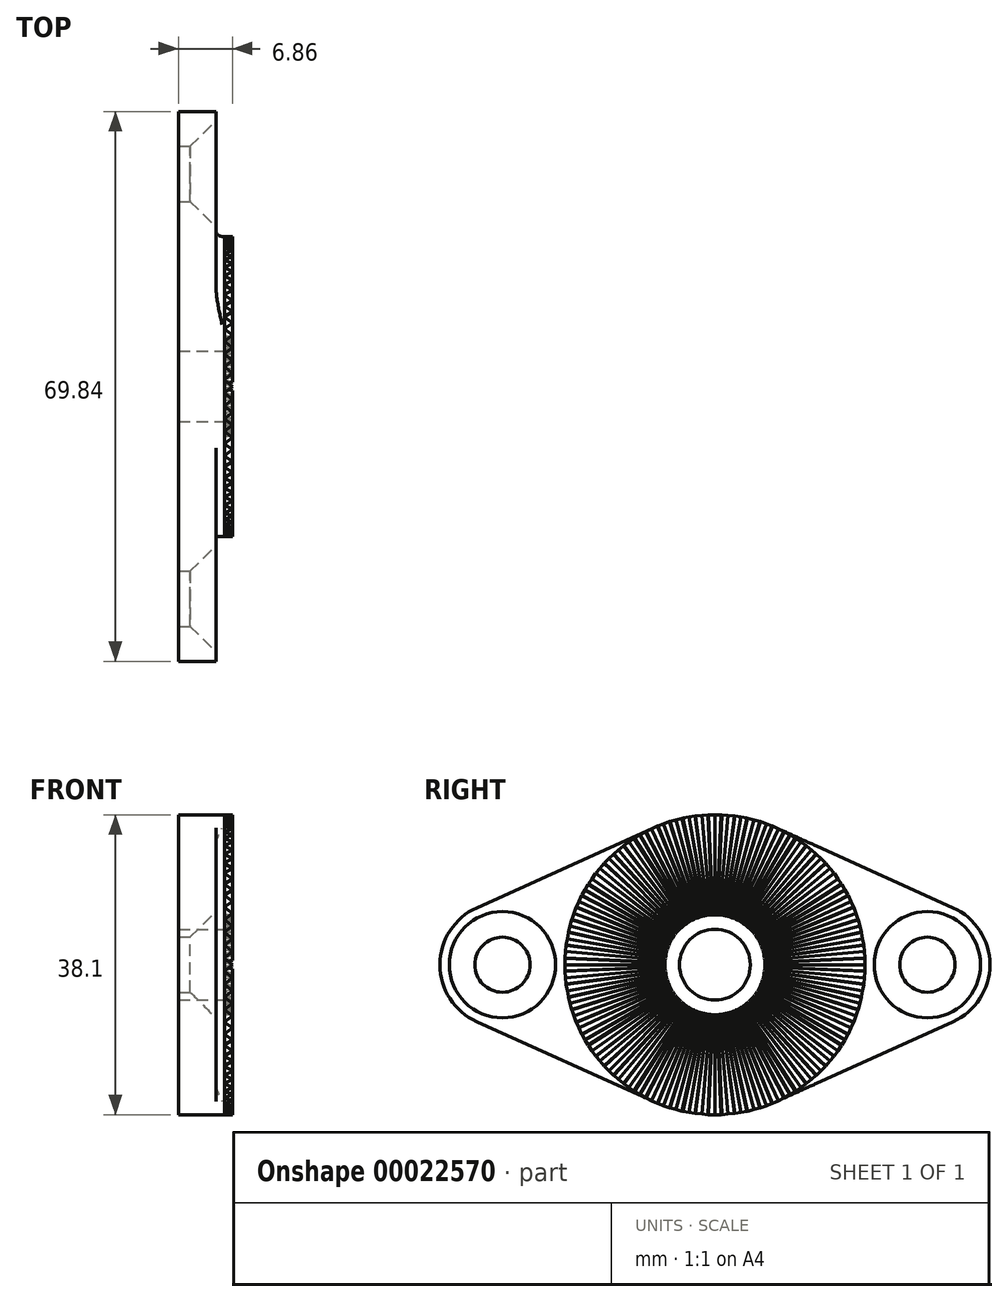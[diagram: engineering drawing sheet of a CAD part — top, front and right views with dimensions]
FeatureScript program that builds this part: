
annotation { "Feature Type Name" : "Feature", "Feature Type Description" : "" }
export const myFeature = defineFeature(function(context is Context, id is Id, definition is map)
    precondition{}
    {
        {
            var Q0;
            Q0=qCreatedBy(makeId("Right.planeOp"),FACE);
            var sketch = newSketch(context, id + "F0", { "sketchPlane" : qUnion([Q0])});
            skArc(sketch, "E0", {"start": v(-7.84, -17.36) * mm, "mid": v(0, -19.05) * mm, "end": v(7.84, -17.36) * mm});
            skLineSegment(sketch, "E1", {"start": v(-77.57, 0) * mm, "end": v(77.57, 0) * mm, "construction": true});
            skArc(sketch, "E2", {"start": v(-30.26, 7.23) * mm, "mid": v(-34.92, 0) * mm, "end": v(-30.26, -7.23) * mm});
            skArc(sketch, "E3", {"start": v(30.26, -7.23) * mm, "mid": v(34.92, 0) * mm, "end": v(30.26, 7.23) * mm});
            skLineSegment(sketch, "E4", {"start": v(-30.26, 7.23) * mm, "end": v(-7.84, 17.36) * mm});
            skLineSegment(sketch, "E5", {"start": v(-30.26, -7.23) * mm, "end": v(-7.84, -17.36) * mm});
            skLineSegment(sketch, "E6", {"start": v(30.26, -7.23) * mm, "end": v(7.84, -17.36) * mm});
            skLineSegment(sketch, "E7", {"start": v(30.26, 7.23) * mm, "end": v(7.84, 17.36) * mm});
            skArc(sketch, "E8.trimOffspring", {"start": v(7.84, 17.36) * mm, "mid": v(0, 19.05) * mm, "end": v(-7.84, 17.36) * mm});
            skSolve(sketch);
        }
        {
            var Q0;
            Q0=qSketchRegion(id+"F0",true);
            extrude(context, id + "F1", {"entities" : qUnion([Q0]), "depth" : 4.76 * mm});
        }
        {
            var Q0;
            Q0=makeQuery(id+"F1.opExtrude","CAP_FACE",FACE,{"disambiguationData":[OSD([sQuery(id+"F0.wireOp",EDGE,"E0"),sQuery(id+"F0.wireOp",EDGE,"E2"),sQuery(id+"F0.wireOp",EDGE,"E3"),sQuery(id+"F0.wireOp",EDGE,"E4"),sQuery(id+"F0.wireOp",EDGE,"E5"),sQuery(id+"F0.wireOp",EDGE,"E6"),sQuery(id+"F0.wireOp",EDGE,"E7"),sQuery(id+"F0.wireOp",EDGE,"E8.trimOffspring")])],"isStart":false});
            var sketch = newSketch(context, id + "F2", { "sketchPlane" : qUnion([Q0])});
            skCircle(sketch, "E9", {"center": v(0, 0) * mm, "radius": 19.05 * mm});
            skSolve(sketch);
        }
        {
            var Q0;
            Q0=qSketchRegion(id+"F2",true);
            extrude(context, id + "F3", {"entities" : qUnion([Q0]), "operationType" : NewBodyOperationType.ADD, "depth" : 1.08 * mm});
        }
        {
            var Q0;
            Q0=qCreatedBy(makeId("Top.planeOp"),FACE);
            cPlane(context, id + "F4", {"entities" : qUnion([Q0]), "cplaneType" : CPlaneType.OFFSET, "offset" : 19.05 * mm, "width" : 152.4 * mm, "height" : 152.4 * mm});
        }
        {
            var Q0;
            Q0=qCreatedBy(makeId("Top.planeOp"),FACE);
            cPlane(context, id + "F5", {"entities" : qUnion([Q0]), "cplaneType" : CPlaneType.OFFSET, "offset" : 6.35 * mm, "width" : 152.4 * mm, "height" : 152.4 * mm});
        }
        {
            var Q0;
            Q0=qCreatedBy(id+"F4.planeOp",FACE);
            var sketch = newSketch(context, id + "F6", { "sketchPlane" : qUnion([Q0])});
            skLineSegment(sketch, "E10", {"start": v(0, 0) * mm, "end": v(5.84, 0) * mm, "construction": true});
            skLineSegment(sketch, "E11", {"start": v(5.84, 0.8) * mm, "end": v(5.84, -0.8) * mm});
            skLineSegment(sketch, "E12", {"start": v(5.84, 0) * mm, "end": v(6.86, 0) * mm, "construction": true});
            skLineSegment(sketch, "E13", {"start": v(5.84, -0.8) * mm, "end": v(6.86, 0) * mm});
            skLineSegment(sketch, "E14", {"start": v(5.84, 0.8) * mm, "end": v(6.86, 0) * mm});
            skSolve(sketch);
        }
        {
            var Q0;
            Q0=qCreatedBy(id+"F5.planeOp",FACE);
            var sketch = newSketch(context, id + "F7", { "sketchPlane" : qUnion([Q0])});
            skLineSegment(sketch, "E15", {"start": v(5.84, -0.25) * mm, "end": v(5.84, 0.25) * mm});
            skLineSegment(sketch, "E16", {"start": v(-1.93, 0) * mm, "end": v(5.84, 0) * mm, "construction": true});
            skLineSegment(sketch, "E17", {"start": v(5.84, 0) * mm, "end": v(6.86, 0) * mm, "construction": true});
            skLineSegment(sketch, "E18", {"start": v(6.86, 0) * mm, "end": v(5.84, 0.25) * mm});
            skLineSegment(sketch, "E19", {"start": v(6.86, 0) * mm, "end": v(5.84, -0.25) * mm});
            skSolve(sketch);
        }
        {
            var Q1;
            Q1=qSketchRegion(id+"F7",true);
            var Q2;
            Q2=qSketchRegion(id+"F6",true);
            loft(context, id + "F8", {"operationType" : NewBodyOperationType.ADD, "sheetProfilesArray" : [{ "sheetProfileEntities" : qUnion([Q1]) }, { "sheetProfileEntities" : qUnion([Q2]) }]});
        }
        {
            var Q0;
            {var subQ0=sQuery(id+"F6.wireOp",EDGE,"E11");var subQ1=sQuery(id+"F6.wireOp",EDGE,"E13");var subQ2=sQuery(id+"F6.wireOp",EDGE,"E14");var subQ3=sQuery(id+"F7.wireOp",EDGE,"E15");var subQ4=sQuery(id+"F7.wireOp",EDGE,"E18");var subQ5=sQuery(id+"F7.wireOp",EDGE,"E19");Q0=makeQuery(id+"F8.opLoft","SWEPT_FACE",FACE,{"disambiguationData":[OSD([subQ0,subQ1,subQ2,subQ3,subQ4,subQ5]),TDD([makeQuery(id+"F6.imprint","INTERSECT",VERTEX,{"derivedFrom":[subQ0,subQ2]}),makeQuery(id+"F6.imprint","INTERSECT",VERTEX,{"derivedFrom":[subQ1,subQ2]}),makeQuery(id+"F6.imprint","IMPRINT",EDGE,{"derivedFrom":subQ2}),makeQuery(id+"F7.imprint","INTERSECT",VERTEX,{"derivedFrom":[subQ3,subQ4]}),makeQuery(id+"F7.imprint","INTERSECT",VERTEX,{"derivedFrom":[subQ4,subQ5]}),makeQuery(id+"F7.imprint","IMPRINT",EDGE,{"derivedFrom":subQ4})])]});}
            var Q1;
            {var subQ0=sQuery(id+"F6.wireOp",EDGE,"E11");var subQ1=sQuery(id+"F6.wireOp",EDGE,"E13");var subQ2=sQuery(id+"F6.wireOp",EDGE,"E14");var subQ3=sQuery(id+"F7.wireOp",EDGE,"E15");var subQ4=sQuery(id+"F7.wireOp",EDGE,"E18");var subQ5=sQuery(id+"F7.wireOp",EDGE,"E19");Q1=makeQuery(id+"F8.opLoft","SWEPT_FACE",FACE,{"disambiguationData":[OSD([subQ0,subQ1,subQ2,subQ3,subQ4,subQ5]),TDD([makeQuery(id+"F6.imprint","INTERSECT",VERTEX,{"derivedFrom":[subQ0,subQ1]}),makeQuery(id+"F6.imprint","INTERSECT",VERTEX,{"derivedFrom":[subQ1,subQ2]}),makeQuery(id+"F6.imprint","IMPRINT",EDGE,{"derivedFrom":subQ1}),makeQuery(id+"F7.imprint","INTERSECT",VERTEX,{"derivedFrom":[subQ3,subQ5]}),makeQuery(id+"F7.imprint","INTERSECT",VERTEX,{"derivedFrom":[subQ4,subQ5]}),makeQuery(id+"F7.imprint","IMPRINT",EDGE,{"derivedFrom":subQ5})])]});}
            var Q2;
            Q2=makeQuery(id+"F8.opLoft","CAP_FACE",FACE,{"disambiguationData":[OSD([makeQuery(id+"F7.imprint","IMPRINT",FACE,{"disambiguationData":[TD([[makeQuery(id+"F7.imprint","IMPRINT",EDGE,{"derivedFrom":sQuery(id+"F7.wireOp",EDGE,"E15")}),-1.0]])]})])],"isStart":true});
            var Q3;
            Q3=makeQuery(id+"F8.opLoft","CAP_FACE",FACE,{"disambiguationData":[OSD([makeQuery(id+"F6.imprint","IMPRINT",FACE,{"disambiguationData":[TD([[makeQuery(id+"F6.imprint","IMPRINT",EDGE,{"derivedFrom":sQuery(id+"F6.wireOp",EDGE,"E11")}),1.0]])]})])],"isStart":true});
            var Q4;
            {var subQ0=sQuery(id+"F6.wireOp",EDGE,"E11");var subQ1=sQuery(id+"F6.wireOp",EDGE,"E13");var subQ2=sQuery(id+"F6.wireOp",EDGE,"E14");var subQ3=sQuery(id+"F7.wireOp",EDGE,"E15");var subQ4=sQuery(id+"F7.wireOp",EDGE,"E18");var subQ5=sQuery(id+"F7.wireOp",EDGE,"E19");var subQ6=makeQuery(id+"F6.imprint","INTERSECT",VERTEX,{"derivedFrom":[subQ0,subQ2]});var subQ7=makeQuery(id+"F6.imprint","IMPRINT",EDGE,{"derivedFrom":subQ0});var subQ8=makeQuery(id+"F7.imprint","INTERSECT",VERTEX,{"derivedFrom":[subQ3,subQ4]});var subQ9=makeQuery(id+"F8.opLoft","SWEPT_FACE",FACE,{"disambiguationData":[OSD([subQ0,subQ1,subQ2,subQ3,subQ4,subQ5]),TDD([subQ6,makeQuery(id+"F6.imprint","INTERSECT",VERTEX,{"derivedFrom":[subQ0,subQ1]}),subQ7,makeQuery(id+"F7.imprint","INTERSECT",VERTEX,{"derivedFrom":[subQ3,subQ5]}),subQ8,makeQuery(id+"F7.imprint","IMPRINT",EDGE,{"derivedFrom":subQ3})])]});var subQ10=makeQuery(id+"F6.imprint","IMPRINT",EDGE,{"derivedFrom":subQ2});Q4=makeQuery(id+"F8.boolean.opBoolean","SPLIT",FACE,{"disambiguationData":[TD([makeQuery(id+"F8.opLoft","SWEPT_FACE",FACE,{"disambiguationData":[OSD([subQ0,subQ1,subQ2,subQ3,subQ4,subQ5]),TDD([subQ6,makeQuery(id+"F6.imprint","INTERSECT",VERTEX,{"derivedFrom":[subQ1,subQ2]}),subQ10,subQ8,makeQuery(id+"F7.imprint","INTERSECT",VERTEX,{"derivedFrom":[subQ4,subQ5]}),makeQuery(id+"F7.imprint","IMPRINT",EDGE,{"derivedFrom":subQ4})])]})])],"derivedFrom":subQ9});}
            var Q5;
            {var subQ0=sQuery(id+"F6.wireOp",EDGE,"E11");var subQ1=sQuery(id+"F6.wireOp",EDGE,"E13");var subQ2=sQuery(id+"F6.wireOp",EDGE,"E14");var subQ3=sQuery(id+"F7.wireOp",EDGE,"E15");var subQ4=sQuery(id+"F7.wireOp",EDGE,"E18");var subQ5=sQuery(id+"F7.wireOp",EDGE,"E19");var subQ6=makeQuery(id+"F6.imprint","INTERSECT",VERTEX,{"derivedFrom":[subQ0,subQ1]});var subQ7=makeQuery(id+"F6.imprint","IMPRINT",EDGE,{"derivedFrom":subQ0});var subQ8=makeQuery(id+"F7.imprint","INTERSECT",VERTEX,{"derivedFrom":[subQ3,subQ5]});var subQ9=makeQuery(id+"F8.opLoft","SWEPT_FACE",FACE,{"disambiguationData":[OSD([subQ0,subQ1,subQ2,subQ3,subQ4,subQ5]),TDD([makeQuery(id+"F6.imprint","INTERSECT",VERTEX,{"derivedFrom":[subQ0,subQ2]}),subQ6,subQ7,subQ8,makeQuery(id+"F7.imprint","INTERSECT",VERTEX,{"derivedFrom":[subQ3,subQ4]}),makeQuery(id+"F7.imprint","IMPRINT",EDGE,{"derivedFrom":subQ3})])]});var subQ10=makeQuery(id+"F6.imprint","IMPRINT",EDGE,{"derivedFrom":subQ1});Q5=makeQuery(id+"F8.boolean.opBoolean","SPLIT",FACE,{"disambiguationData":[TD([makeQuery(id+"F8.opLoft","SWEPT_FACE",FACE,{"disambiguationData":[OSD([subQ0,subQ1,subQ2,subQ3,subQ4,subQ5]),TDD([subQ6,makeQuery(id+"F6.imprint","INTERSECT",VERTEX,{"derivedFrom":[subQ1,subQ2]}),subQ10,subQ8,makeQuery(id+"F7.imprint","INTERSECT",VERTEX,{"derivedFrom":[subQ4,subQ5]}),makeQuery(id+"F7.imprint","IMPRINT",EDGE,{"derivedFrom":subQ5})])]})])],"derivedFrom":subQ9});}
            var Q6;
            Q6=makeQuery(id+"F3.boolean.opBoolean","MERGE",FACE,{"derivedFrom":[makeQuery(id+"F1.opExtrude","SWEPT_FACE",FACE,{"disambiguationData":[OSD([sQuery(id+"F0.wireOp",EDGE,"E0")])]}),makeQuery(id+"F1.opExtrude","SWEPT_FACE",FACE,{"disambiguationData":[OSD([sQuery(id+"F0.wireOp",EDGE,"E8.trimOffspring")])]}),makeQuery(id+"F3.opExtrude","SWEPT_FACE",FACE,{"disambiguationData":[OSD([sQuery(id+"F2.wireOp",EDGE,"E9")])]})]});
            circularPattern(context, id + "F9", {"operationType" : NewBodyOperationType.ADD, "faces" : qUnion([Q0, Q1, Q2, Q3, Q4, Q5]), "axis" : qUnion([Q6]), "angle" : 360 * degree, "instanceCount" : round(72), "equalSpace" : true, "patternType" : PatternType.FACE});
        }
        {
            var Q0;
            {var subQ0=sQuery(id+"F0.wireOp",EDGE,"E0");var subQ1=sQuery(id+"F0.wireOp",EDGE,"E3");var subQ2=sQuery(id+"F0.wireOp",EDGE,"E6");var subQ3=sQuery(id+"F0.wireOp",EDGE,"E7");var subQ4=sQuery(id+"F0.wireOp",EDGE,"E8.trimOffspring");Q0=makeQuery(id+"F3.boolean.opBoolean","SPLIT",FACE,{"disambiguationData":[TD([makeQuery(id+"F1.opExtrude","SWEPT_FACE",FACE,{"disambiguationData":[OSD([subQ1])]})])],"derivedFrom":makeQuery(id+"F1.opExtrude","CAP_FACE",FACE,{"disambiguationData":[OSD([subQ0,sQuery(id+"F0.wireOp",EDGE,"E2"),subQ1,sQuery(id+"F0.wireOp",EDGE,"E4"),sQuery(id+"F0.wireOp",EDGE,"E5"),subQ2,subQ3,subQ4])],"isStart":false})});}
            var sketch = newSketch(context, id + "F10", { "sketchPlane" : qUnion([Q0])});
            skCircle(sketch, "E20", {"center": v(26.99, 0) * mm, "radius": 3.5 * mm});
            skCircle(sketch, "E21", {"center": v(-26.99, 0) * mm, "radius": 3.5 * mm});
            skCircle(sketch, "E22", {"center": v(0, 0) * mm, "radius": 4.5 * mm});
            skSolve(sketch);
        }
        {
            var Q0;
            Q0=qSketchRegion(id+"F10",true);
            extrude(context, id + "F11", {"entities" : qUnion([Q0]), "operationType" : NewBodyOperationType.REMOVE, "endBound" : BoundingType.SYMMETRIC, "oppositeDirection" : true, "depth" : 25.4 * mm});
        }
        {
            var Q0;
            Q0=makeQuery(id+"F10.imprint","IMPRINT",FACE,{"disambiguationData":[TD([[makeQuery(id+"F10.imprint","IMPRINT",EDGE,{"derivedFrom":sQuery(id+"F10.wireOp",EDGE,"E20")}),-1.0]])]});
            var sketch = newSketch(context, id + "F12", { "sketchPlane" : qUnion([Q0])});
            skCircle(sketch, "E23", {"center": v(26.99, 0) * mm, "radius": 6.75 * mm});
            skCircle(sketch, "E24", {"center": v(-26.99, 0) * mm, "radius": 6.75 * mm});
            skSolve(sketch);
        }
        {
            var Q0;
            Q0=qSketchRegion(id+"F12",true);
            extrude(context, id + "F13", {"entities" : qUnion([Q0]), "operationType" : NewBodyOperationType.REMOVE, "oppositeDirection" : true, "depth" : 25.4 * mm, "hasDraft" : true, "draftAngle" : 45 * degree, "draftPullDirection" : true});
        }
        {
            var Q0;
            {var subQ0=sQuery(id+"F2.wireOp",EDGE,"E9");var subQ3=sQuery(id+"F0.wireOp",EDGE,"E6");Q0=makeQuery(id+"F3.boolean.opBoolean","SPLIT",EDGE,{"disambiguationData":[TD([makeQuery(id+"F1.opExtrude","SWEPT_FACE",FACE,{"disambiguationData":[OSD([subQ3])]})])],"derivedFrom":makeQuery(id+"F3.opExtrude","CAP_EDGE",EDGE,{"disambiguationData":[OSD([subQ0])],"isStart":true})});}
            var Q1;
            {var subQ0=sQuery(id+"F2.wireOp",EDGE,"E9");var subQ3=sQuery(id+"F0.wireOp",EDGE,"E4");Q1=makeQuery(id+"F3.boolean.opBoolean","SPLIT",EDGE,{"disambiguationData":[TD([makeQuery(id+"F1.opExtrude","SWEPT_FACE",FACE,{"disambiguationData":[OSD([subQ3])]})])],"derivedFrom":makeQuery(id+"F3.opExtrude","CAP_EDGE",EDGE,{"disambiguationData":[OSD([subQ0])],"isStart":true})});}
            fillet(context, id + "F14", {"entities" : qUnion([Q0, Q1]), "radius" : 0.8 * mm, "allowEdgeOverflow" : false});
        }
    });
